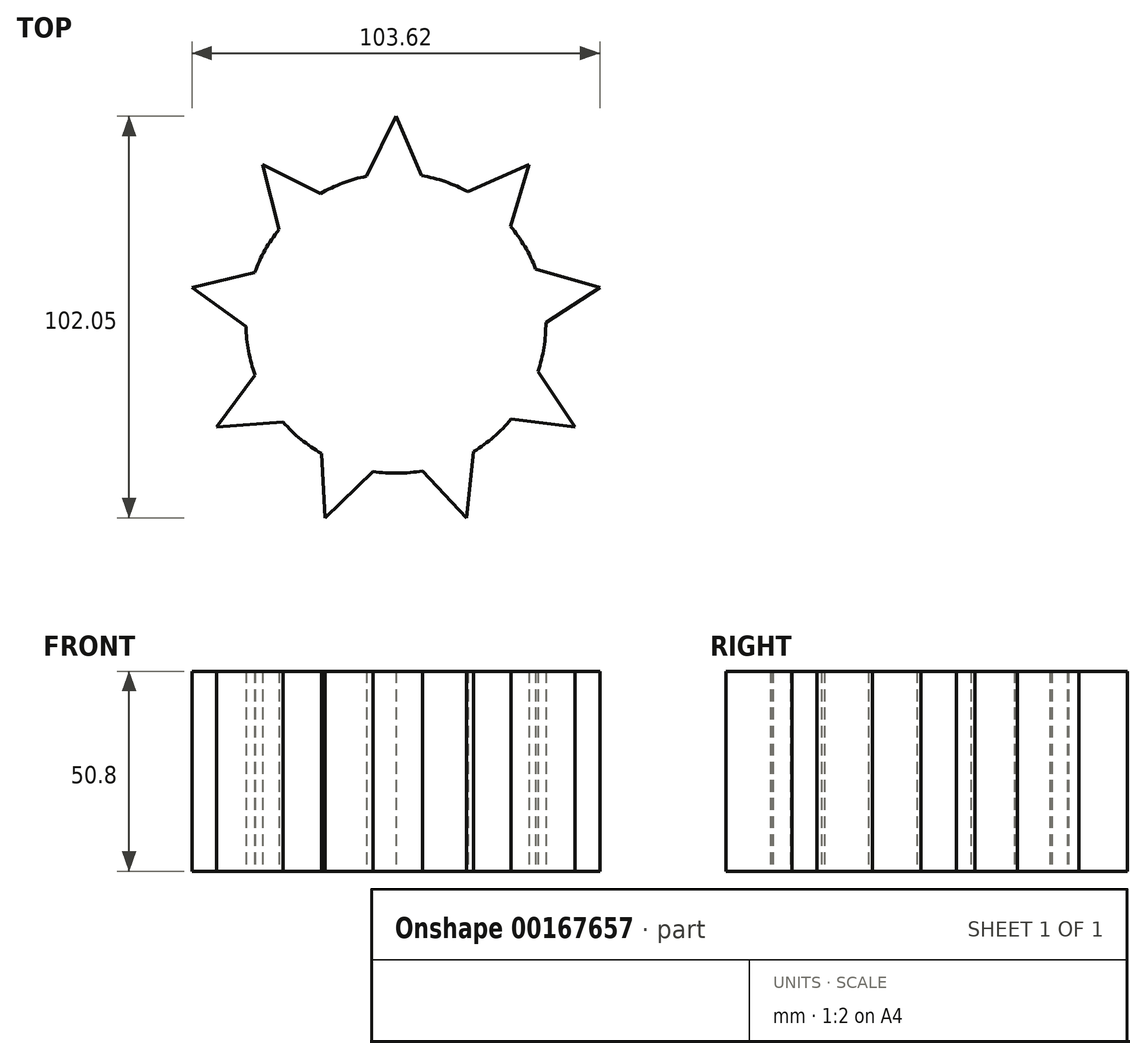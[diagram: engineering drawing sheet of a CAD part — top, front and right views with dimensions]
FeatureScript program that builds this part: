
annotation { "Feature Type Name" : "Feature", "Feature Type Description" : "" }
export const myFeature = defineFeature(function(context is Context, id is Id, definition is map)
    precondition{}
    {
        {
            var Q0;
            Q0=qCreatedBy(makeId("Top.planeOp"),FACE);
            var sketch = newSketch(context, id + "F0", { "sketchPlane" : qUnion([Q0])});
            skCircle(sketch, "E0", {"center": v(0, 0) * mm, "radius": 38.1 * mm});
            skLineSegment(sketch, "E1", {"start": v(0, 52.61) * mm, "end": v(-7.43, 37.37) * mm});
            skLineSegment(sketch, "E2", {"start": v(-7.43, 37.37) * mm, "end": v(0, 52.61) * mm});
            skLineSegment(sketch, "E3", {"start": v(0, 52.61) * mm, "end": v(6.46, 37.55) * mm});
            skLineSegment(sketch, "E4", {"start": v(6.46, 37.55) * mm, "end": v(-7.43, 37.37) * mm});
            skLineSegment(sketch, "E5.1.0", {"start": v(-33.82, 40.3) * mm, "end": v(-19.19, 32.92) * mm});
            skLineSegment(sketch, "E5.1.1", {"start": v(-19.19, 32.92) * mm, "end": v(-29.71, 23.85) * mm});
            skLineSegment(sketch, "E5.1.2", {"start": v(-29.71, 23.85) * mm, "end": v(-33.82, 40.3) * mm});
            skLineSegment(sketch, "E5.2.0", {"start": v(-51.81, 9.14) * mm, "end": v(-35.86, 12.88) * mm});
            skLineSegment(sketch, "E5.2.1", {"start": v(-35.86, 12.88) * mm, "end": v(-38.1, -0.83) * mm});
            skLineSegment(sketch, "E5.2.2", {"start": v(-38.1, -0.83) * mm, "end": v(-51.81, 9.14) * mm});
            skLineSegment(sketch, "E5.3.0", {"start": v(-45.57, -26.3) * mm, "end": v(-35.75, -13.18) * mm});
            skLineSegment(sketch, "E5.3.1", {"start": v(-35.75, -13.18) * mm, "end": v(-28.64, -25.12) * mm});
            skLineSegment(sketch, "E5.3.2", {"start": v(-28.64, -25.12) * mm, "end": v(-45.57, -26.3) * mm});
            skLineSegment(sketch, "E5.4.0", {"start": v(-18, -49.44) * mm, "end": v(-18.91, -33.07) * mm});
            skLineSegment(sketch, "E5.4.1", {"start": v(-18.91, -33.07) * mm, "end": v(-5.8, -37.66) * mm});
            skLineSegment(sketch, "E5.4.2", {"start": v(-5.8, -37.66) * mm, "end": v(-18, -49.44) * mm});
            skLineSegment(sketch, "E5.5.0", {"start": v(18, -49.44) * mm, "end": v(6.77, -37.5) * mm});
            skLineSegment(sketch, "E5.5.1", {"start": v(6.77, -37.5) * mm, "end": v(19.77, -32.57) * mm});
            skLineSegment(sketch, "E5.5.2", {"start": v(19.77, -32.57) * mm, "end": v(18, -49.44) * mm});
            skLineSegment(sketch, "E5.6.0", {"start": v(45.57, -26.3) * mm, "end": v(29.29, -24.37) * mm});
            skLineSegment(sketch, "E5.6.1", {"start": v(29.29, -24.37) * mm, "end": v(36.08, -12.25) * mm});
            skLineSegment(sketch, "E5.6.2", {"start": v(36.08, -12.25) * mm, "end": v(45.57, -26.3) * mm});
            skLineSegment(sketch, "E5.7.0", {"start": v(51.81, 9.14) * mm, "end": v(38.1, 0.16) * mm});
            skLineSegment(sketch, "E5.7.1", {"start": v(38.1, 0.16) * mm, "end": v(35.5, 13.8) * mm});
            skLineSegment(sketch, "E5.7.2", {"start": v(35.5, 13.8) * mm, "end": v(51.81, 9.14) * mm});
            skLineSegment(sketch, "E5.8.0", {"start": v(33.82, 40.3) * mm, "end": v(29.08, 24.61) * mm});
            skLineSegment(sketch, "E5.8.1", {"start": v(29.08, 24.61) * mm, "end": v(18.32, 33.4) * mm});
            skLineSegment(sketch, "E5.8.2", {"start": v(18.32, 33.4) * mm, "end": v(33.82, 40.3) * mm});
            skLineSegment(sketch, "E5.anchor1", {"start": v(0, 0) * mm, "end": v(6.46, 37.55) * mm, "construction": true});
            skLineSegment(sketch, "E5.anchor2", {"start": v(0, 0) * mm, "end": v(6.46, 37.55) * mm, "construction": true});
            skSolve(sketch);
        }
        {
            var Q0;
            Q0 = qSketchRegion(id + "F0", true);
            extrude(context, id + "F1", {"entities" : qUnion([Q0]), "depth" : 50.8 * mm});
        }
    });
